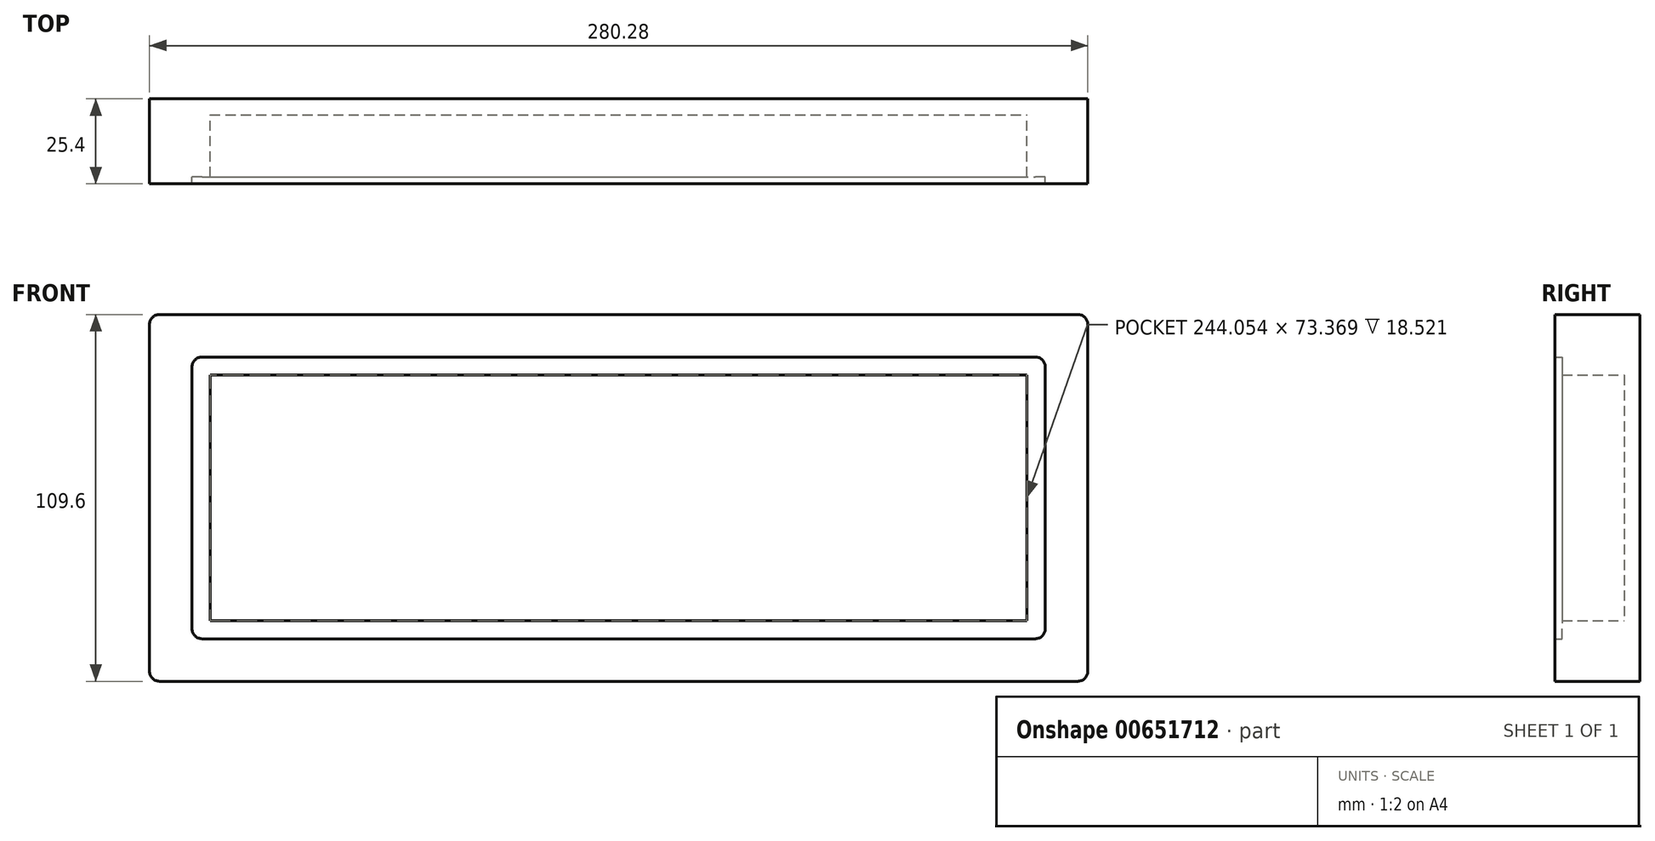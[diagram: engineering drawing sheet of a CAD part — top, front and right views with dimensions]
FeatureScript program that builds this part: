
annotation { "Feature Type Name" : "Feature", "Feature Type Description" : "" }
export const myFeature = defineFeature(function(context is Context, id is Id, definition is map)
    precondition{}
    {
        {
            var Q0;
            Q0=qCreatedBy(makeId("Front.planeOp"),FACE);
            var sketch = newSketch(context, id + "F0", { "sketchPlane" : qUnion([Q0])});
            skLineSegment(sketch, "E0.bottom", {"start": v(-137.14, 54.8) * mm, "end": v(137.14, 54.8) * mm});
            skLineSegment(sketch, "E0.top", {"start": v(-137.14, -54.8) * mm, "end": v(137.14, -54.8) * mm});
            skLineSegment(sketch, "E0.left", {"start": v(-140.14, 51.8) * mm, "end": v(-140.14, -51.8) * mm});
            skLineSegment(sketch, "E0.right", {"start": v(140.14, 51.8) * mm, "end": v(140.14, -51.8) * mm});
            skPoint(sketch, "E0.middle", {"position": v(0, 0) * mm});
            skLineSegment(sketch, "E1.bottom", {"start": v(-124.44, 42.1) * mm, "end": v(124.44, 42.1) * mm});
            skLineSegment(sketch, "E1.top", {"start": v(-124.44, -42.1) * mm, "end": v(124.44, -42.1) * mm});
            skLineSegment(sketch, "E1.left", {"start": v(-127.44, 39.1) * mm, "end": v(-127.44, -39.1) * mm});
            skLineSegment(sketch, "E1.right", {"start": v(127.44, 39.1) * mm, "end": v(127.44, -39.1) * mm});
            skLineSegment(sketch, "E2.bottom", {"start": v(-122.03, 36.68) * mm, "end": v(122.03, 36.68) * mm});
            skLineSegment(sketch, "E2.top", {"start": v(-122.03, -36.68) * mm, "end": v(122.03, -36.68) * mm});
            skLineSegment(sketch, "E2.left", {"start": v(-122.03, 36.68) * mm, "end": v(-122.03, -36.68) * mm});
            skLineSegment(sketch, "E2.right", {"start": v(122.03, 36.68) * mm, "end": v(122.03, -36.68) * mm});
            skPoint(sketch, "E3.visualSharp", {"position": v(-127.44, 42.1) * mm});
            skArc(sketch, "E3.filletArc", {"start": v(-124.44, 42.1) * mm, "mid": v(-126.56, 41.22) * mm, "end": v(-127.44, 39.1) * mm});
            skPoint(sketch, "E4.visualSharp", {"position": v(-127.44, -42.1) * mm});
            skArc(sketch, "E4.filletArc", {"start": v(-127.44, -39.1) * mm, "mid": v(-126.56, -41.22) * mm, "end": v(-124.44, -42.1) * mm});
            skPoint(sketch, "E5.visualSharp", {"position": v(127.44, 42.1) * mm});
            skArc(sketch, "E5.filletArc", {"start": v(127.44, 39.1) * mm, "mid": v(126.56, 41.22) * mm, "end": v(124.44, 42.1) * mm});
            skPoint(sketch, "E6.visualSharp", {"position": v(127.44, -42.1) * mm});
            skArc(sketch, "E6.filletArc", {"start": v(124.44, -42.1) * mm, "mid": v(126.56, -41.22) * mm, "end": v(127.44, -39.1) * mm});
            skPoint(sketch, "E7.visualSharp", {"position": v(-140.14, 54.8) * mm});
            skArc(sketch, "E7.filletArc", {"start": v(-137.14, 54.8) * mm, "mid": v(-139.26, 53.92) * mm, "end": v(-140.14, 51.8) * mm});
            skPoint(sketch, "E8.visualSharp", {"position": v(-140.14, -54.8) * mm});
            skArc(sketch, "E8.filletArc", {"start": v(-140.14, -51.8) * mm, "mid": v(-139.26, -53.92) * mm, "end": v(-137.14, -54.8) * mm});
            skPoint(sketch, "E9.visualSharp", {"position": v(140.14, 54.8) * mm});
            skArc(sketch, "E9.filletArc", {"start": v(140.14, 51.8) * mm, "mid": v(139.26, 53.92) * mm, "end": v(137.14, 54.8) * mm});
            skPoint(sketch, "E10.visualSharp", {"position": v(140.14, -54.8) * mm});
            skArc(sketch, "E10.filletArc", {"start": v(137.14, -54.8) * mm, "mid": v(139.26, -53.92) * mm, "end": v(140.14, -51.8) * mm});
            skSolve(sketch);
        }
        {
            var Q0;
            Q0=makeQuery(id+"F0.imprint","IMPRINT",FACE,{"disambiguationData":[TD([[makeQuery(id+"F0.imprint","IMPRINT",EDGE,{"derivedFrom":sQuery(id+"F0.wireOp",EDGE,"E0.bottom")}),-1.0]])]});
            extrude(context, id + "F1", {"entities" : qUnion([Q0]), "depth" : 25.4 * mm, "offsetDistance" : 25.4 * mm});
        }
        {
            var Q0;
            Q0=makeQuery(id+"F0.imprint","IMPRINT",FACE,{"disambiguationData":[TD([[makeQuery(id+"F0.imprint","IMPRINT",EDGE,{"derivedFrom":sQuery(id+"F0.wireOp",EDGE,"E1.bottom")}),-1.0]])]});
            extrude(context, id + "F2", {"entities" : qUnion([Q0]), "operationType" : NewBodyOperationType.ADD, "depth" : 23.28 * mm, "offsetDistance" : 25.4 * mm});
        }
        {
            var Q0;
            Q0=makeQuery(id+"F0.imprint","IMPRINT",FACE,{"disambiguationData":[TD([[makeQuery(id+"F0.imprint","IMPRINT",EDGE,{"derivedFrom":sQuery(id+"F0.wireOp",EDGE,"E2.bottom")}),-1.0]])]});
            extrude(context, id + "F3", {"entities" : qUnion([Q0]), "operationType" : NewBodyOperationType.ADD, "depth" : 4.76 * mm, "offsetDistance" : 25.4 * mm});
        }
    });
